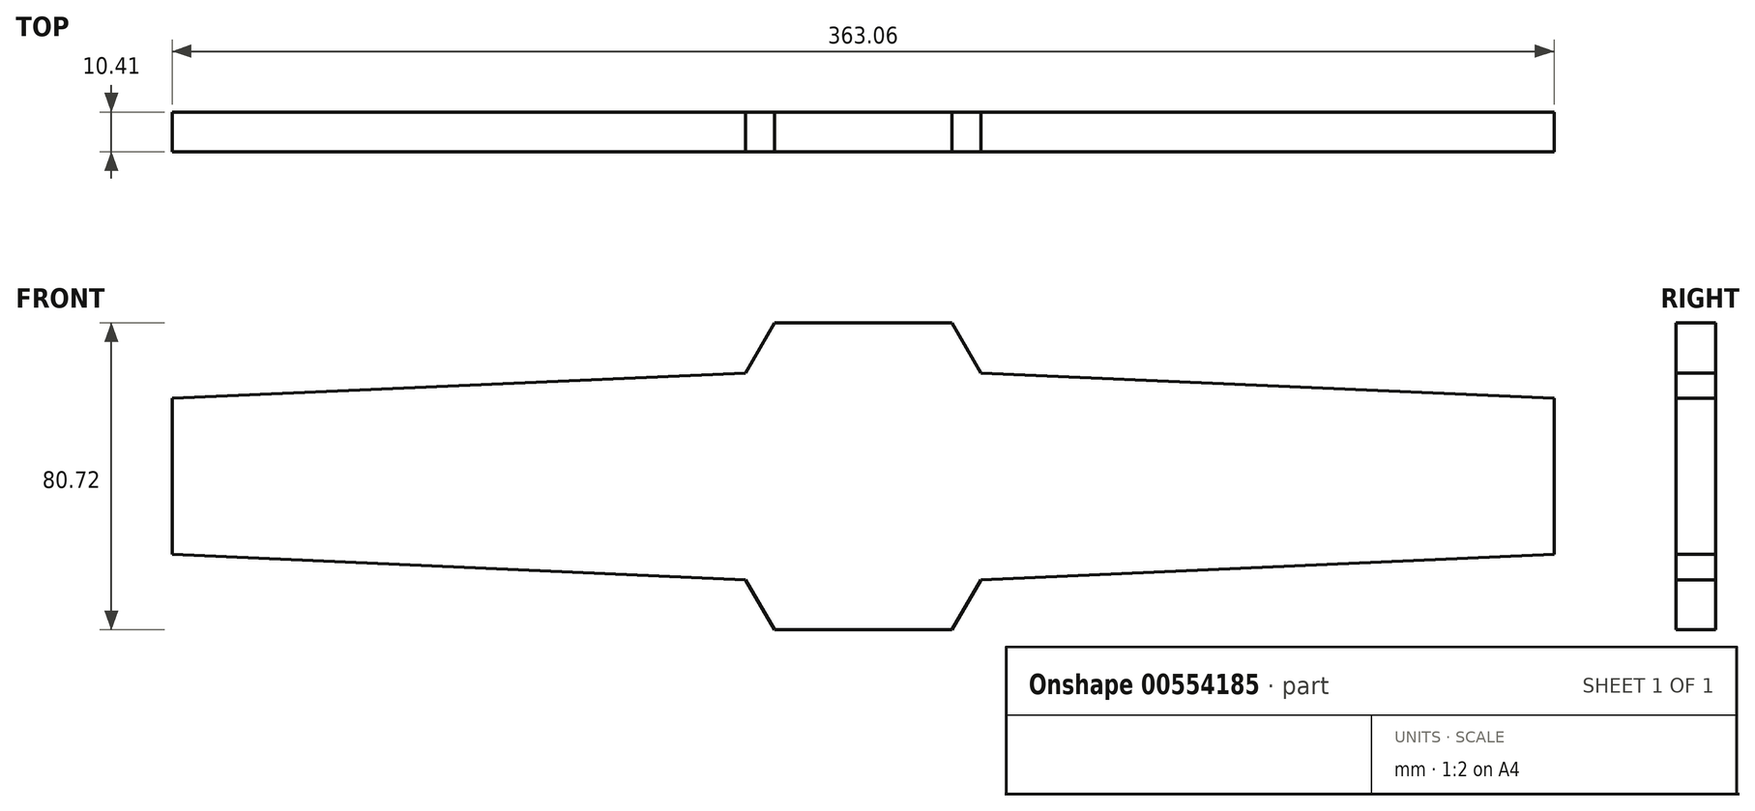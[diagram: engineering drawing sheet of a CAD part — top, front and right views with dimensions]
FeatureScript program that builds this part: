
annotation { "Feature Type Name" : "Feature", "Feature Type Description" : "" }
export const myFeature = defineFeature(function(context is Context, id is Id, definition is map)
    precondition{}
    {
        {
            var Q0;
            Q0=qCreatedBy(makeId("Front.planeOp"),FACE);
            var sketch = newSketch(context, id + "F0", { "sketchPlane" : qUnion([Q0])});
            skLineSegment(sketch, "E0.0", {"start": v(23.3, -40.36) * mm, "end": v(-23.3, -40.36) * mm});
            skLineSegment(sketch, "E0.1", {"start": v(-23.3, -40.36) * mm, "end": v(-30.9, -27.2) * mm});
            skLineSegment(sketch, "E0.2", {"start": v(-30.9, 27.2) * mm, "end": v(-23.3, 40.36) * mm});
            skLineSegment(sketch, "E0.3", {"start": v(-23.3, 40.36) * mm, "end": v(23.3, 40.36) * mm});
            skLineSegment(sketch, "E0.4", {"start": v(23.3, 40.36) * mm, "end": v(30.9, 27.2) * mm});
            skLineSegment(sketch, "E0.5", {"start": v(30.9, -27.2) * mm, "end": v(23.3, -40.36) * mm});
            skPoint(sketch, "E0.0.midPoint", {"position": v(0, -40.36) * mm});
            skLineSegment(sketch, "E1", {"start": v(30.9, 27.2) * mm, "end": v(181.53, 20.49) * mm});
            skLineSegment(sketch, "E2", {"start": v(181.53, 20.49) * mm, "end": v(181.53, 0) * mm});
            skLineSegment(sketch, "E3.MirrorCS", {"start": v(30.9, -27.2) * mm, "end": v(181.53, -20.49) * mm});
            skLineSegment(sketch, "E4.MirrorCS", {"start": v(181.53, -20.49) * mm, "end": v(181.53, 0) * mm});
            skLineSegment(sketch, "E5.MirrorCS", {"start": v(-30.9, 27.2) * mm, "end": v(-181.53, 20.49) * mm});
            skLineSegment(sketch, "E6.MirrorCS", {"start": v(-30.9, -27.2) * mm, "end": v(-181.53, -20.49) * mm});
            skLineSegment(sketch, "E7.MirrorCS", {"start": v(-181.53, -20.49) * mm, "end": v(-181.53, 0) * mm});
            skLineSegment(sketch, "E8.MirrorCS", {"start": v(-181.53, 20.49) * mm, "end": v(-181.53, 0) * mm});
            skPoint(sketch, "E9.orphan", {"position": v(-46.6, 0) * mm});
            skPoint(sketch, "E0.cCircle.center.orphan", {"position": v(0, 0) * mm});
            skSolve(sketch);
        }
        {
            var Q0;
            Q0=makeQuery(id+"F0.imprint","IMPRINT",FACE,{"disambiguationData":[TD([[makeQuery(id+"F0.imprint","IMPRINT",EDGE,{"derivedFrom":sQuery(id+"F0.wireOp",EDGE,"E0.0")}),-1.0]])]});
            extrude(context, id + "F1", {"entities" : qUnion([Q0]), "depth" : 10.4 * mm, "offsetDistance" : 25.4 * mm});
        }
    });
